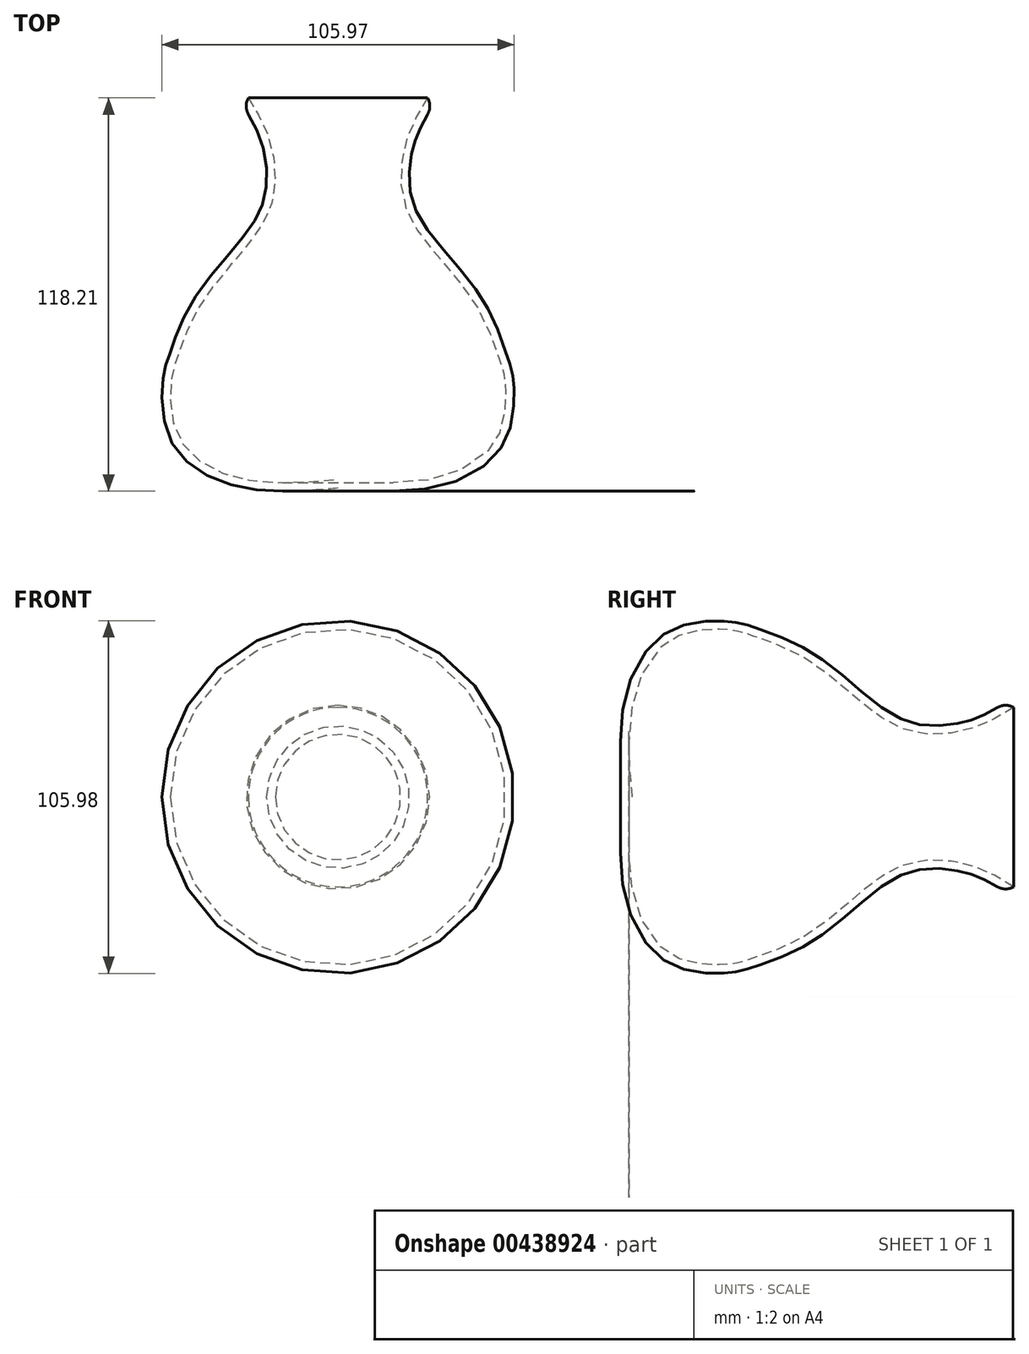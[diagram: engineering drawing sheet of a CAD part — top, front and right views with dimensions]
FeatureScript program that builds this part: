
annotation { "Feature Type Name" : "Feature", "Feature Type Description" : "" }
export const myFeature = defineFeature(function(context is Context, id is Id, definition is map)
    precondition{}
    {
        {
            var Q0;
            Q0=qCreatedBy(makeId("Top.planeOp"),FACE);
            var sketch = newSketch(context, id + "F0", { "sketchPlane" : qUnion([Q0])});
            skLineSegment(sketch, "E0", {"start": v(0, 61.19) * mm, "end": v(0, -56) * mm});
            skLineSegment(sketch, "E1", {"start": v(0, 61.19) * mm, "end": v(-29.9, 61.19) * mm});
            skFitSpline(sketch, "E2", {"points": [v(-29.9, 61.19) * mm, v(-23.56, 49.41) * mm, v(-21.64, 33.68) * mm, v(-27.49, 20.72) * mm, v(-43.8, 0) * mm, v(-50.75, -16.13) * mm, v(-52.56, -22.47) * mm, v(-50.14, -42.1) * mm, v(-29.9, -55.7) * mm, v(0, -56) * mm], "startDerivative": vector(69.04, -120.93) * mm, "endDerivative": vector(213.98, 19.6) * mm});
            skSolve(sketch);
        }
        {
            var Q0;
            Q0=makeQuery(id+"F0.imprint","IMPRINT",FACE,{"disambiguationData":[TD([[makeQuery(id+"F0.imprint","IMPRINT",EDGE,{"derivedFrom":sQuery(id+"F0.wireOp",EDGE,"E0")}),-1.0]])]});
            var Q1;
            Q1=sQuery(id+"F0.wireOp",EDGE,"E0");
            revolve(context, id + "F1", {"entities" : qUnion([Q0]), "axis" : qUnion([Q1]), "revolveType" : RevolveType.FULL});
        }
        {
            var Q0;
            Q0=makeQuery(id+"F1.opRevolve","SWEPT_FACE",FACE,{"disambiguationData":[OSD([sQuery(id+"F0.wireOp",EDGE,"E1")])]});
            shell(context, id + "F2", {"entities" : qUnion([Q0]), "thickness" : 2.54 * mm});
        }
        {
            var Q0;
            Q0=makeQuery(id+"F1.opRevolve","SWEPT_EDGE",EDGE,{"disambiguationData":[OSD([sQuery(id+"F0.wireOp",EDGE,"E1"),sQuery(id+"F0.wireOp",EDGE,"E2")])]});
            fillet(context, id + "F3", {"entities" : qUnion([Q0]), "radius" : 5.08 * mm, "tangentPropagation" : true, "allowEdgeOverflow" : false});
        }
    });
